# Revit family: KEUCO_59547000170_
name_source: partatom
category: Generic Models
revit_build: Autodesk Revit 2016 (Build: 20150220_1215(x64)
units: mm (PartAtom-declared; Revit-internal decimal feet)

## family parameters
Always vertical = No
Can host rebar = No
Cut with Voids When Loaded = No
Part Type = Normal
Room Calculation Point = No
Round Connector Dimension = Use Diameter
Shared = No
Work Plane-Based = Yes

## types (1)
- 59547000170
    Artikelnummer = 59547000170
    Ausschreibungstext = KEUCO UP Funktionseinheit Universal DN15, 59547000170
zur einfachen Installation von Produkten mit G1/2 Zoll,
schallentkoppelt,
Anschluss in Kombination mit der Montageschiene,
Innengewinde G1/2 Zoll, Einbautiefe 80 mm - 110 mm

Hinweis:
Universell einsetzbar für Produkte mit 1/2 Zoll Anschluss.
    Breite = 45 mm  [stored 0.147638 ft]
    Default Elevation = 1219 mm
    Description = zur einfachen Installation von Produkten mit 1/2 Zoll
Anschluss in Kombination mit der Montageschiene,
Innengewinde G1/2, Einbautiefe 80 - 110 mm
    Gewicht = 0
    Kategorie = ARM
    Manufacturer = KEUCO
    Material = Stahl, verchromt
    Serie = Plan
    URL = https://www.keuco.com
    Verwendung = DU / WA / ZU

note: [stored X ft] marks values corroborated as IEEE doubles in the binary element streams (Revit-internal decimal feet)

## geometry (parser evidence)
native form markers: Sweep x3
no freeform markers — native parametric forms only
